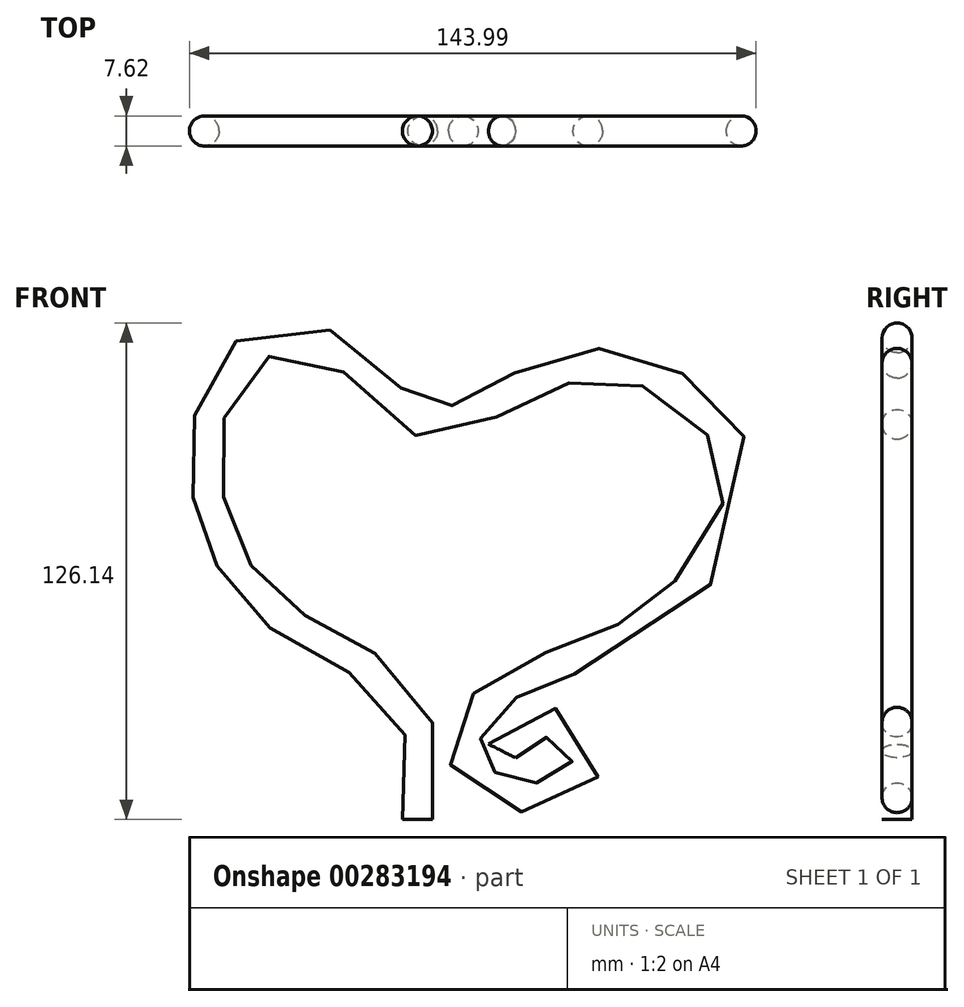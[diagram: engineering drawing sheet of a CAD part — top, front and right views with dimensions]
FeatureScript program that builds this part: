
annotation { "Feature Type Name" : "Feature", "Feature Type Description" : "" }
export const myFeature = defineFeature(function(context is Context, id is Id, definition is map)
    precondition{}
    {
        {
            var Q0;
            Q0=qCreatedBy(makeId("Top.planeOp"),FACE);
            var sketch = newSketch(context, id + "F0", { "sketchPlane" : qUnion([Q0])});
            skCircle(sketch, "E0", {"center": v(0, 0) * mm, "radius": 3.81 * mm});
            skSolve(sketch);
        }
        {
            var Q0;
            Q0=qCreatedBy(makeId("Front.planeOp"),FACE);
            var sketch = newSketch(context, id + "F1", { "sketchPlane" : qUnion([Q0])});
            skFitSpline(sketch, "E1", {"points": [v(0, 0) * mm, v(0, 24.17) * mm, v(-12.34, 38.75) * mm, v(-28.65, 47.48) * mm, v(-43.45, 59.7) * mm, v(-51.73, 76.64) * mm, v(-53.86, 96.71) * mm, v(-42.87, 119.23) * mm, v(-19.29, 118.69) * mm, v(0, 101.47) * mm, v(13.7, 103.16) * mm, v(31.78, 112.6) * mm, v(52.24, 115.5) * mm, v(72.05, 104.88) * mm, v(82.28, 85.65) * mm, v(70.54, 60.8) * mm, v(56.36, 48.3) * mm, v(40.58, 41.2) * mm, v(22.1, 33.67) * mm, v(13.31, 23.92) * mm, v(12.64, 13.48) * mm, v(25.85, 5.88) * mm, v(40.12, 9.1) * mm, v(42.33, 19.95) * mm, v(29.54, 24.47) * mm, v(21.49, 17.43) * mm], "startDerivative": vector(77.28, 562.23) * mm, "endDerivative": vector(-210.07, -303.2) * mm});
            skSolve(sketch);
        }
        {
            var Q0;
            Q0=makeQuery(id+"F0.imprint","IMPRINT",FACE,{"disambiguationData":[TD([[makeQuery(id+"F0.imprint","IMPRINT",EDGE,{"derivedFrom":sQuery(id+"F0.wireOp",EDGE,"E0")}),1.0]])]});
            var Q1;
            Q1=sQuery(id+"F1.wireOp",EDGE,"E1");
            sweep(context, id + "F2", {"profiles" : qUnion([Q0]), "path" : qUnion([Q1])});
        }
    });
